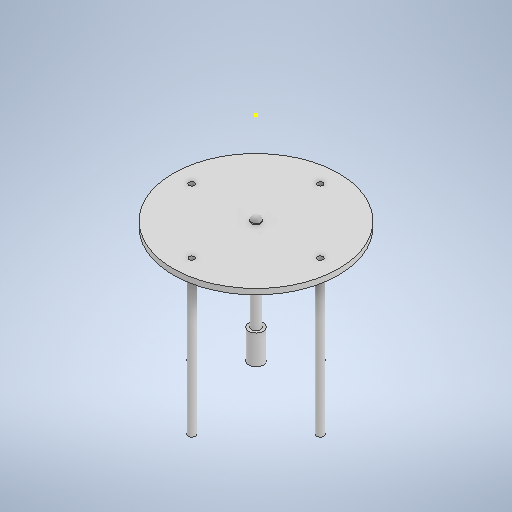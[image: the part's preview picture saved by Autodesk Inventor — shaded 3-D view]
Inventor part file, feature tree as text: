
AUTODESK INVENTOR PART (.ipt)
format: ipt  version: 2025 (Build 290162000, 162)  size: 307,712 bytes
history: native  units: mm
features: sketch x11, extrude x9, other x1, fillet x1
ambient origin geometry x8: Origin, YZ Plane, XZ Plane, XY Plane, X Axis, Y Axis, Z Axis, Center Point
bodies: Body1 (feature_tree)
feature tree (22):
  other  "Bryła1"
  extrude  "Wyciągnięcie proste1"  Depth=90.0mm
  extrude  "Wyciągnięcie proste3"  Depth=3.0mm TaperAngle=0.0deg
  extrude  "Wyciągnięcie proste4"  Depth=10.0mm TaperAngle=0.0deg
  extrude  "Wyciągnięcie proste5"  Depth=5.0mm
  sketch  "Szkic8"
  extrude  "Wyciągnięcie proste6"  Depth=100.0mm TaperAngle=0.0deg
  extrude  "Wyciągnięcie proste7"  Depth=4.0mm
  sketch  "Szkic13"
  extrude  "Wyciągnięcie proste8"  Depth=2.0mm TaperAngle=0.0deg
  fillet  "Zaokrąglenie2"  Radius=8.0mm
  extrude  "Wyciągnięcie proste9"  Depth=16.0mm TaperAngle=0.0deg
  extrude  "Wyciągnięcie proste10"  Depth=10.0mm TaperAngle=0.0deg
  sketch  "Szkic1"
  sketch  "Szkic2"
  sketch  "Szkic3"
  sketch  "Szkic4"
  sketch  "Szkic9"
  sketch  "Szkic12"
  sketch  "Szkic14"
  sketch  "Szkic17"
  sketch  "Szkic18"
